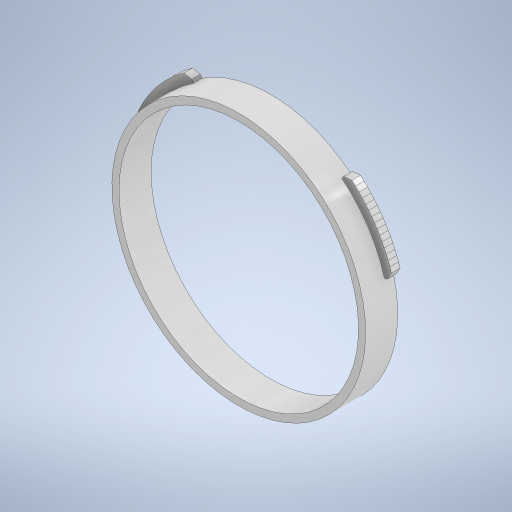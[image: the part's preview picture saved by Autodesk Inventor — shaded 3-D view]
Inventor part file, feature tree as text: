
AUTODESK INVENTOR PART (.ipt)
format: ipt  version: 2023 (Build 270158000, 158)  size: 4,699,136 bytes
history: native  units: mm
features: other x3, extrude x2, sketch x1
ambient origin geometry x8: Origin, YZ Plane, XZ Plane, XY Plane, X Axis, Y Axis, Z Axis, Center Point
bodies: Solido1 (feature_tree)
feature tree (6):
  other  "Sony_E-Mount_Body_Cap"
  sketch  "Schizzo1"
  extrude  "Estrusione1"  Depth=5.5mm TaperAngle=0.0deg
  extrude  "Estrusione2"  Depth=1.5mm TaperAngle=0.0deg
  other  "Composto1"
  other  "Superf1"
